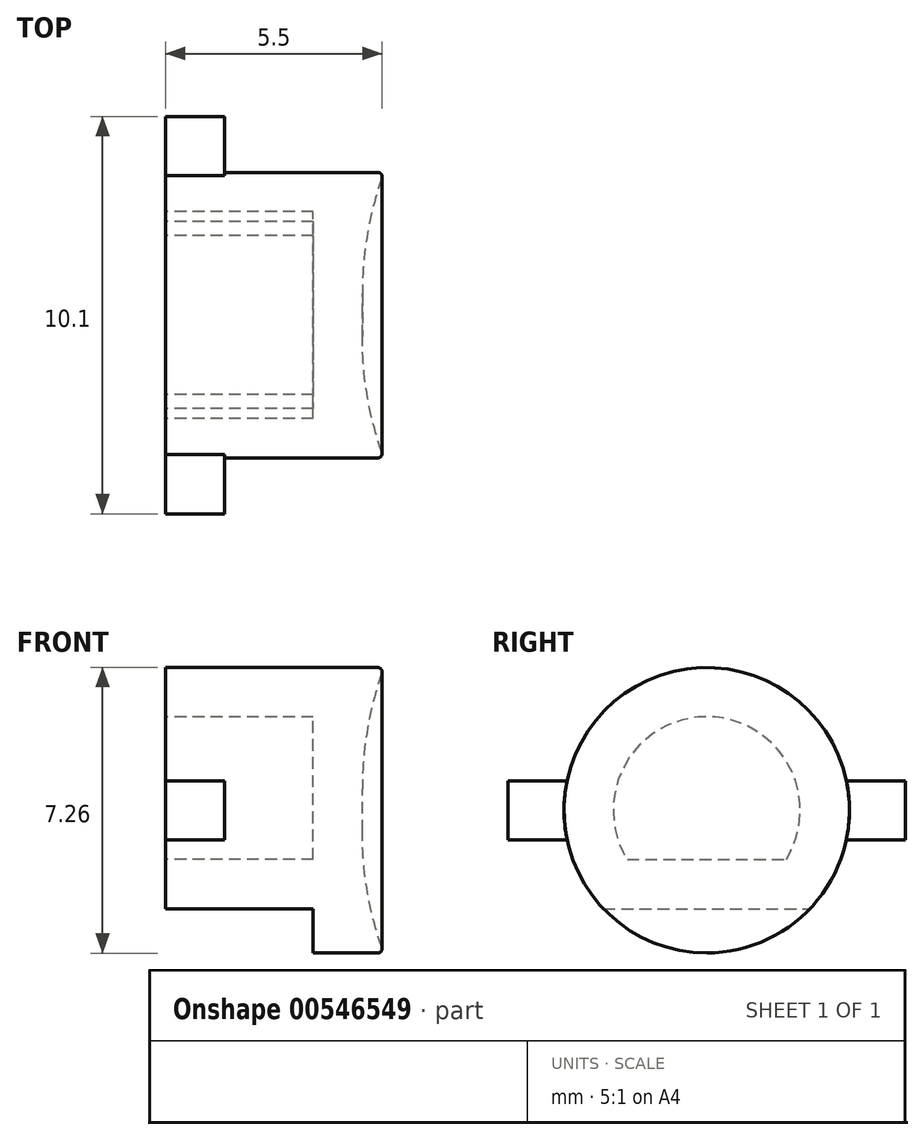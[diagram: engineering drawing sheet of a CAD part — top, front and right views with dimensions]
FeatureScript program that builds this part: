
annotation { "Feature Type Name" : "Feature", "Feature Type Description" : "" }
export const myFeature = defineFeature(function(context is Context, id is Id, definition is map)
    precondition{}
    {
        {
            var Q0;
            Q0=qCreatedBy(makeId("Right.planeOp"),FACE);
            var sketch = newSketch(context, id + "F0", { "sketchPlane" : qUnion([Q0])});
            skCircle(sketch, "E0", {"center": v(0, 0) * mm, "radius": 3.62 * mm});
            skSolve(sketch);
        }
        {
            var Q0;
            Q0=makeQuery(id+"F0.imprint","IMPRINT",FACE,{"disambiguationData":[TD([[makeQuery(id+"F0.imprint","IMPRINT",EDGE,{"derivedFrom":sQuery(id+"F0.wireOp",EDGE,"E0")}),1.0]])]});
            extrude(context, id + "F1", {"entities" : qUnion([Q0]), "endBound" : BoundingType.SYMMETRIC, "depth" : 5.5 * mm, "offsetDistance" : 25 * mm});
        }
        {
            var Q0;
            Q0=makeQuery(id+"F1.opExtrude","CAP_FACE",FACE,{"disambiguationData":[OSD([sQuery(id+"F0.wireOp",EDGE,"E0")])],"isStart":true});
            var sketch = newSketch(context, id + "F2", { "sketchPlane" : qUnion([Q0])});
            skLineSegment(sketch, "E1.left", {"start": v(5.05, -0.75) * mm, "end": v(5.05, 0.75) * mm});
            skLineSegment(sketch, "E2.left", {"start": v(-5.05, 0.75) * mm, "end": v(-5.05, -0.75) * mm});
            skLineSegment(sketch, "E3", {"start": v(5.05, 0.75) * mm, "end": v(3.55, 0.75) * mm});
            skLineSegment(sketch, "E4", {"start": v(5.05, -0.75) * mm, "end": v(3.55, -0.75) * mm});
            skArc(sketch, "E5", {"start": v(-3.55, 0.75) * mm, "mid": v(-3.63, 0) * mm, "end": v(-3.55, -0.75) * mm});
            skLineSegment(sketch, "E6", {"start": v(-5.05, 0.75) * mm, "end": v(-3.55, 0.75) * mm});
            skLineSegment(sketch, "E7", {"start": v(-5.05, -0.75) * mm, "end": v(-3.55, -0.75) * mm});
            skArc(sketch, "E8.trimOffspring", {"start": v(3.55, -0.75) * mm, "mid": v(3.63, 0) * mm, "end": v(3.55, 0.75) * mm});
            skPoint(sketch, "E9", {"position": v(5.05, 0) * mm});
            skPoint(sketch, "E10", {"position": v(-5.05, 0) * mm});
            skSolve(sketch);
        }
        {
            var Q0;
            Q0=qSketchRegion(id+"F2",true);
            extrude(context, id + "F3", {"entities" : qUnion([Q0]), "operationType" : NewBodyOperationType.ADD, "oppositeDirection" : true, "depth" : 1.5 * mm, "offsetDistance" : 25 * mm});
        }
        {
            var Q0;
            Q0=makeQuery(id+"F1.opExtrude","CAP_FACE",FACE,{"disambiguationData":[OSD([sQuery(id+"F0.wireOp",EDGE,"E0")])],"isStart":false});
            var sketch = newSketch(context, id + "F4", { "sketchPlane" : qUnion([Q0])});
            skCircle(sketch, "E11", {"center": v(0, 0) * mm, "radius": 3.5 * mm});
            skSolve(sketch);
        }
        {
            var Q0;
            Q0=qSketchRegion(id+"F4",true);
            extrude(context, id + "F5", {"entities" : qUnion([Q0]), "operationType" : NewBodyOperationType.REMOVE, "oppositeDirection" : true, "depth" : .5 * mm, "offsetDistance" : 25 * mm});
        }
        {
            var Q0;
            Q0=makeQuery(id+"F3.boolean.opBoolean","MERGE",FACE,{"derivedFrom":[makeQuery(id+"F1.opExtrude","CAP_FACE",FACE,{"disambiguationData":[OSD([sQuery(id+"F0.wireOp",EDGE,"E0")])],"isStart":true}),makeQuery(id+"F3.opExtrude","CAP_FACE",FACE,{"disambiguationData":[OSD([sQuery(id+"F2.wireOp",EDGE,"E1.left"),sQuery(id+"F2.wireOp",EDGE,"E3"),sQuery(id+"F2.wireOp",EDGE,"E4"),sQuery(id+"F2.wireOp",EDGE,"E8.trimOffspring")])],"isStart":true}),makeQuery(id+"F3.opExtrude","CAP_FACE",FACE,{"disambiguationData":[OSD([sQuery(id+"F2.wireOp",EDGE,"E2.left"),sQuery(id+"F2.wireOp",EDGE,"E5"),sQuery(id+"F2.wireOp",EDGE,"E6"),sQuery(id+"F2.wireOp",EDGE,"E7")])],"isStart":true})]});
            var sketch = newSketch(context, id + "F6", { "sketchPlane" : qUnion([Q0])});
            skArc(sketch, "E12", {"start": v(-2.62, -2.5) * mm, "mid": v(0, -3.63) * mm, "end": v(2.63, -2.5) * mm});
            skLineSegment(sketch, "E13", {"start": v(2.63, -2.5) * mm, "end": v(-2.62, -2.5) * mm});
            skSolve(sketch);
        }
        {
            var Q0;
            Q0=qSketchRegion(id+"F6",true);
            extrude(context, id + "F7", {"entities" : qUnion([Q0]), "operationType" : NewBodyOperationType.REMOVE, "oppositeDirection" : true, "depth" : 3.75 * mm, "offsetDistance" : 25 * mm});
        }
        {
            var Q0;
            Q0=makeQuery(id+"F1.opExtrude","CAP_FACE",FACE,{"disambiguationData":[OSD([sQuery(id+"F0.wireOp",EDGE,"E0")])],"isStart":true});
            shell(context, id + "F8", {"entities" : qUnion([Q0]), "thickness" : 1.25 * mm});
        }
        {
            var Q0;
            Q0=makeQuery(id+"F5.boolean.opBoolean","COPY",FACE,{"derivedFrom":makeQuery(id+"F5.opExtrude","CAP_FACE",FACE,{"disambiguationData":[OSD([sQuery(id+"F4.wireOp",EDGE,"E11")])],"isStart":false})});
            fillet(context, id + "F9", {"entities" : qUnion([Q0]), "radius" : 9 * mm, "tangentPropagation" : true, "allowEdgeOverflow" : false});
        }
        {
            var Q0;
            Q0=makeQuery(id+"F9.opFillet","BLEND_EDGE",EDGE,{"blendedFrom":[makeQuery(id+"F5.boolean.opBoolean","COPY",EDGE,{"derivedFrom":makeQuery(id+"F5.opExtrude","CAP_EDGE",EDGE,{"disambiguationData":[OSD([sQuery(id+"F4.wireOp",EDGE,"E11")])],"isStart":false})}),makeQuery(id+"F1.opExtrude","CAP_FACE",FACE,{"disambiguationData":[OSD([sQuery(id+"F0.wireOp",EDGE,"E0")])],"isStart":false})],"blendedInto":[makeQuery(id+"F1.opExtrude","CAP_FACE",FACE,{"disambiguationData":[OSD([sQuery(id+"F0.wireOp",EDGE,"E0")])],"isStart":false})]});
            var Q1;
            Q1=makeQuery(id+"F1.opExtrude","CAP_EDGE",EDGE,{"disambiguationData":[OSD([sQuery(id+"F0.wireOp",EDGE,"E0")])],"isStart":false});
            fillet(context, id + "F10", {"entities" : qUnion([Q0, Q1]), "radius" : .1 * mm, "tangentPropagation" : true, "allowEdgeOverflow" : false});
        }
    });
